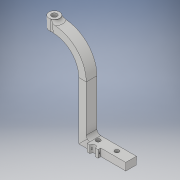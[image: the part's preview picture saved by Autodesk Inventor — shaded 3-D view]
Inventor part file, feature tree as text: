
AUTODESK INVENTOR PART (.ipt)
format: ipt  version: 2017 (Build 210142000, 142)  size: 228,864 bytes
history: native  units: in
note: dims shown in document units (in); Inventor stores cm internally (conversion verified against a paired STEP export)
features: sketch x7, extrude x3, fillet x2, revolve x1, plane x1, sweep x1, hole x1, projected_geometry x1
ambient origin geometry x8: Origin, YZ Plane, XZ Plane, XY Plane, X Axis, Y Axis, Z Axis, Center Point
bodies: Solid1 (feature_tree)
feature tree (17):
  revolve  "Revolution1"  [1 undecoded]
  plane  "Work Plane1"
  sweep  "Sweep1"
  fillet  "Fillet1"  Radius=0.1875in
  hole  "Hole1"  [1 undecoded]
  fillet  "Fillet2"  Radius=1.5in
  extrude  "Extrusion1"  Depth=2.0in
  extrude  "Extrusion2"  Depth=0.15in
  extrude  "Extrusion3"  Depth=0.18in
  sketch  "Sketch1"  dims[d0=0.12in d1=0.13in]
  sketch  "Sketch2"  dims[d2=0.13in d3=90.0deg d4=0.1875in]
  projected_geometry  "Projected Loop1"
  sketch  "Sketch3"  dims[d5=0.16in d6=0.2in d7=1.5in]
  sketch  "Sketch4"  dims[d8=2.5in d9=2.0in]
  sketch  "Sketch5"  dims[d10=0.0in d11=0.0in d12=0.15in]
  sketch  "Sketch6"  dims[d13=0.45in]
  sketch  "Sketch7"  dims[d14=0.205in d15=0.75in d16=0.375in d17=0.25in d18=0.5635in d19=1.0in d20=0.8108in d21=0.18in d22=0.26in d23=0.36in d24=0.0in d25=0.86in d26=0.0in d27=0.52in d28=0.0in]
note: 2 required parameter values undecoded (feature->parameter linkage not recoverable at this tier; creation-order binding heuristic only, values carry confidence <= 0.55)